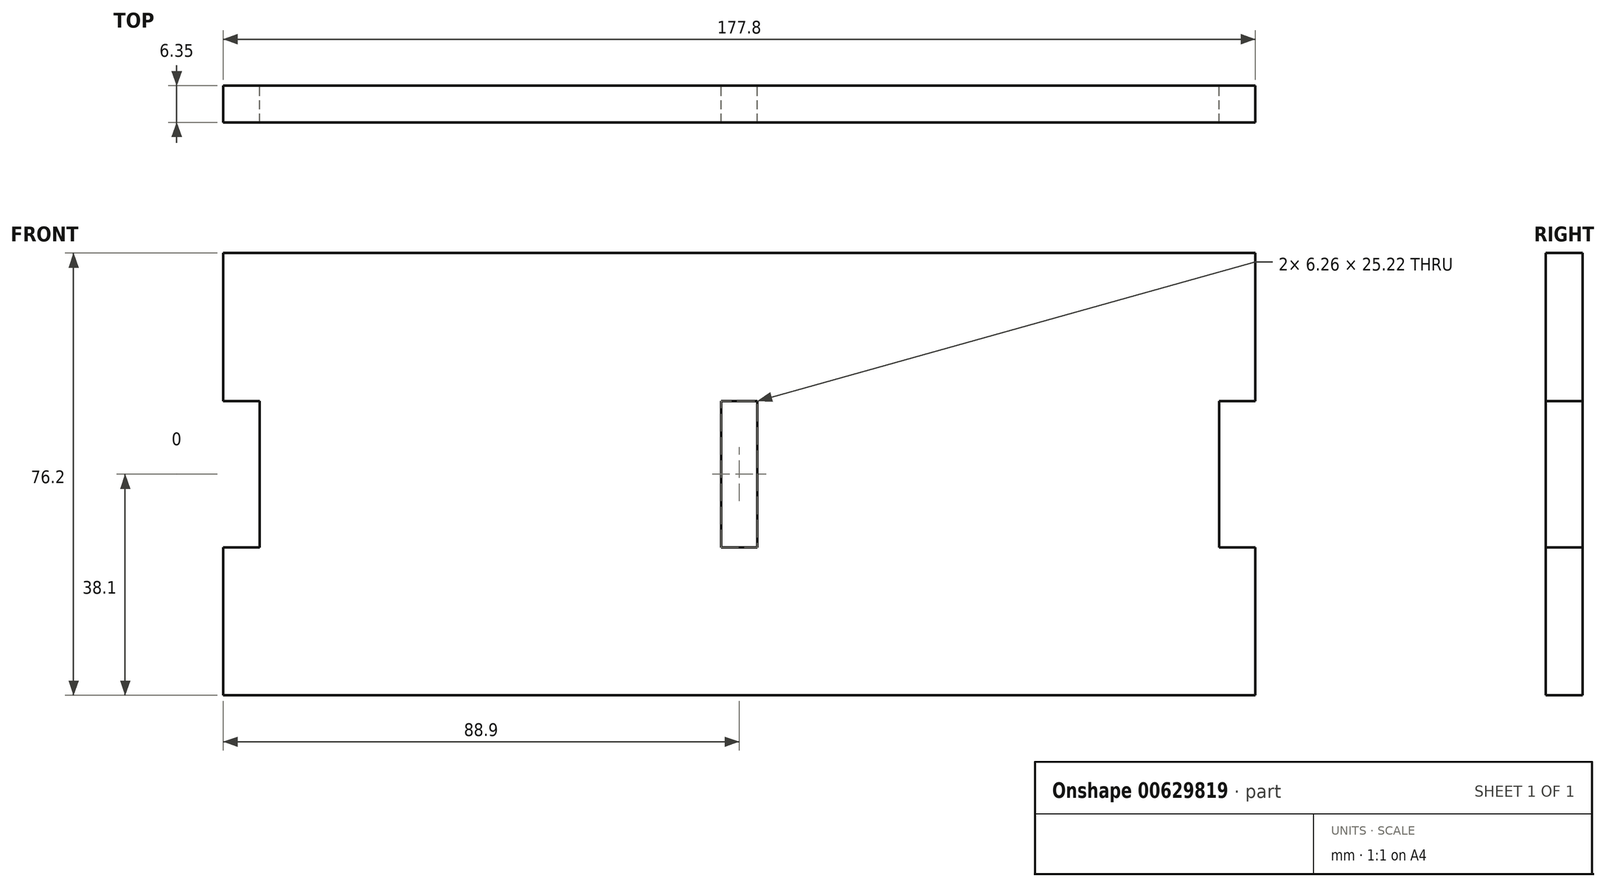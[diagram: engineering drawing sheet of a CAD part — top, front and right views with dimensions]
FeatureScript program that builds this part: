
annotation { "Feature Type Name" : "Feature", "Feature Type Description" : "" }
export const myFeature = defineFeature(function(context is Context, id is Id, definition is map)
    precondition{}
    {
        {
            var Q0;
            Q0=qCreatedBy(makeId("Front.planeOp"),FACE);
            var sketch = newSketch(context, id + "F0", { "sketchPlane" : qUnion([Q0])});
            skLineSegment(sketch, "E0.bottom", {"start": v(0, 0) * mm, "end": v(177.8, 0) * mm});
            skLineSegment(sketch, "E0.top", {"start": v(0, 76.2) * mm, "end": v(177.8, 76.2) * mm});
            skLineSegment(sketch, "E0.left", {"start": v(0, 0) * mm, "end": v(0, 76.2) * mm});
            skLineSegment(sketch, "E0.right", {"start": v(177.8, 0) * mm, "end": v(177.8, 76.2) * mm});
            skLineSegment(sketch, "E1.bottom", {"start": v(25.31, 0) * mm, "end": v(50.89, 0) * mm});
            skLineSegment(sketch, "E1.top", {"start": v(25.31, -6.44) * mm, "end": v(50.89, -6.44) * mm});
            skLineSegment(sketch, "E1.left", {"start": v(25.31, 0) * mm, "end": v(25.31, -6.44) * mm});
            skLineSegment(sketch, "E1.right", {"start": v(50.89, 0) * mm, "end": v(50.89, -6.44) * mm});
            skLineSegment(sketch, "E2.bottom", {"start": v(76.11, 0) * mm, "end": v(101.69, 0) * mm});
            skLineSegment(sketch, "E2.top", {"start": v(76.11, -6.44) * mm, "end": v(101.69, -6.44) * mm});
            skLineSegment(sketch, "E2.left", {"start": v(76.11, 0) * mm, "end": v(76.11, -6.44) * mm});
            skLineSegment(sketch, "E2.right", {"start": v(101.69, 0) * mm, "end": v(101.69, -6.44) * mm});
            skLineSegment(sketch, "E3.bottom", {"start": v(126.91, 0) * mm, "end": v(152.49, 0) * mm});
            skLineSegment(sketch, "E3.top", {"start": v(126.91, -6.44) * mm, "end": v(152.49, -6.44) * mm});
            skLineSegment(sketch, "E3.left", {"start": v(126.91, 0) * mm, "end": v(126.91, -6.44) * mm});
            skLineSegment(sketch, "E3.right", {"start": v(152.49, 0) * mm, "end": v(152.49, -6.44) * mm});
            skPoint(sketch, "E4", {"position": v(38.1, 0) * mm});
            skPoint(sketch, "E5", {"position": v(88.9, 0) * mm});
            skPoint(sketch, "E6", {"position": v(139.7, 0) * mm});
            skLineSegment(sketch, "E7.bottom", {"start": v(0, 50.71) * mm, "end": v(6.26, 50.71) * mm});
            skLineSegment(sketch, "E7.top", {"start": v(0, 25.49) * mm, "end": v(6.26, 25.49) * mm});
            skLineSegment(sketch, "E7.left", {"start": v(0, 50.71) * mm, "end": v(0, 25.49) * mm});
            skLineSegment(sketch, "E7.right", {"start": v(6.26, 50.71) * mm, "end": v(6.26, 25.49) * mm});
            skLineSegment(sketch, "E8.bottom", {"start": v(177.8, 50.71) * mm, "end": v(171.54, 50.71) * mm});
            skLineSegment(sketch, "E8.top", {"start": v(177.8, 25.49) * mm, "end": v(171.54, 25.49) * mm});
            skLineSegment(sketch, "E8.left", {"start": v(177.8, 50.71) * mm, "end": v(177.8, 25.49) * mm});
            skLineSegment(sketch, "E8.right", {"start": v(171.54, 50.71) * mm, "end": v(171.54, 25.49) * mm});
            skPoint(sketch, "E9", {"position": v(0, 38.1) * mm});
            skPoint(sketch, "E10", {"position": v(177.8, 38.1) * mm});
            skLineSegment(sketch, "E11.bottom", {"start": v(85.77, 50.71) * mm, "end": v(92.03, 50.71) * mm});
            skLineSegment(sketch, "E11.top", {"start": v(85.77, 25.49) * mm, "end": v(92.03, 25.49) * mm});
            skLineSegment(sketch, "E11.left", {"start": v(85.77, 50.71) * mm, "end": v(85.77, 25.49) * mm});
            skLineSegment(sketch, "E11.right", {"start": v(92.03, 50.71) * mm, "end": v(92.03, 25.49) * mm});
            skPoint(sketch, "E12", {"position": v(88.9, 50.71) * mm});
            skSolve(sketch);
        }
        {
            var Q0;
            {var subQ2=sQuery(id+"F0.wireOp",EDGE,"E0.top");Q0=makeQuery(id+"F0.imprint","IMPRINT",FACE,{"disambiguationData":[TD([[makeQuery(id+"F0.imprint","IMPRINT",EDGE,{"derivedFrom":subQ2}),-1.0]])]});}
            var Q1;
            Q1=makeQuery(id+"F0.imprint","IMPRINT",FACE,{"disambiguationData":[TD([[makeQuery(id+"F0.imprint","IMPRINT",EDGE,{"derivedFrom":sQuery(id+"F0.wireOp",EDGE,"E1.bottom")}),-1.0]])]});
            var Q2;
            Q2=makeQuery(id+"F0.imprint","IMPRINT",FACE,{"disambiguationData":[TD([[makeQuery(id+"F0.imprint","IMPRINT",EDGE,{"derivedFrom":sQuery(id+"F0.wireOp",EDGE,"E2.bottom")}),-1.0]])]});
            var Q3;
            Q3=makeQuery(id+"F0.imprint","IMPRINT",FACE,{"disambiguationData":[TD([[makeQuery(id+"F0.imprint","IMPRINT",EDGE,{"derivedFrom":sQuery(id+"F0.wireOp",EDGE,"E3.bottom")}),-1.0]])]});
            extrude(context, id + "F1", {"entities" : qUnion([Q0, Q1, Q2, Q3]), "depth" : 6.35 * mm, "offsetDistance" : 25.4 * mm});
        }
    });
